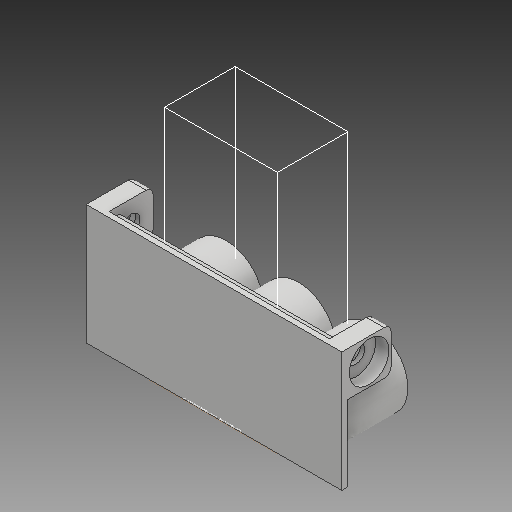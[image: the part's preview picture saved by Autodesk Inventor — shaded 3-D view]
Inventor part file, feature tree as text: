
AUTODESK INVENTOR PART (.ipt)
format: ipt  version: 2018 (Build 220112000, 112)  size: 880,640 bytes
history: native  units: mm
features: sketch x33, extrude x29, fillet x3
ambient origin geometry x8: Origin, YZ Plane, XZ Plane, XY Plane, X Axis, Y Axis, Z Axis, Center Point
bodies: Solid1 (feature_tree)
feature tree (65):
  extrude  "Extrusion1"  Depth=80.0mm
  extrude  "Extrusion2"  Depth=12.0mm
  sketch  "Sketch3"  dims[d5=12.0mm d6=14.5mm]
  extrude  "Extrusion3"  Depth=12.0mm
  extrude  "Extrusion4"  Depth=2.0mm
  extrude  "Extrusion5"  Depth=0.5mm TaperAngle=0.0deg
  sketch  "Sketch7"  dims[d15=10.0mm d16=25.0mm]
  extrude  "Extrusion6"  Depth=25.0mm
  extrude  "Extrusion7"  Depth=25.0mm
  extrude  "Extrusion8"  Depth=10.0mm
  fillet  "Fillet1"  Radius=10.0mm
  fillet  "Fillet2"  Radius=10.0mm
  extrude  "Extrusion9"  Depth=7.5mm TaperAngle=0.0deg
  extrude  "Extrusion10"  Depth=3.0mm
  fillet  "Fillet3"  Radius=3.0mm
  extrude  "Extrusion11"  Depth=21.0mm
  extrude  "Extrusion12"  Depth=41.0mm
  extrude  "Extrusion13"  Depth=42.0mm
  extrude  "Extrusion14"  Depth=38.0mm
  extrude  "Extrusion15"  Depth=45.0mm TaperAngle=0.0deg
  extrude  "Extrusion16"  Depth=3.0mm TaperAngle=0.0deg
  extrude  "Extrusion17"  Depth=3.0mm
  extrude  "Extrusion18"  Depth=39.5mm
  extrude  "Extrusion19"  Depth=45.0mm
  extrude  "Extrusion20"  Depth=125.0mm
  extrude  "Extrusion21"  Depth=1.0mm
  sketch  "Sketch24"  dims[d65=66.0mm d66=3.5mm d67=0.0mm]
  extrude  "Extrusion22"  Depth=10.0mm TaperAngle=0.0deg
  extrude  "Extrusion23"  Depth=12.0mm
  extrude  "Extrusion24"  Depth=3.5mm TaperAngle=0.0deg
  extrude  "Extrusion25"  Depth=2.0mm
  extrude  "Extrusion26"  Depth=2.0mm TaperAngle=0.0deg
  sketch  "Sketch30"  dims[d81=4.0mm]
  extrude  "Extrusion27"  Depth=16.0mm
  extrude  "Extrusion28"  Depth=2.0mm
  extrude  "Extrusion29"  Depth=3.5mm TaperAngle=0.0deg
  sketch  "Sketch1"  dims[d0=145.0mm d1=80.0mm]
  sketch  "Sketch2"  dims[d2=3.0mm d3=0.0mm d4=12.0mm]
  sketch  "Sketch4"  dims[d7=2.0mm d8=2.0mm]
  sketch  "Sketch5"  dims[d9=6.0mm d10=0.0mm d11=0.5mm d12=0.0mm]
  sketch  "Sketch6"  dims[d13=10.0mm d14=25.0mm]
  sketch  "Sketch8"  dims[d17=25.0mm d18=0.0mm d19=22.5mm d20=10.0mm d21=0.0mm d22=10.0mm]
  sketch  "Sketch9"  dims[d23=2.5mm d24=0.0mm d25=7.5mm d26=0.0mm]
  sketch  "Sketch10"  dims[d27=10.0mm d28=0.0mm d29=4.0mm d30=3.0mm]
  sketch  "Sketch11"  dims[d31=1.0mm d32=21.0mm]
  sketch  "Sketch12"  dims[d33=38.0mm d34=41.0mm]
  sketch  "Sketch13"  dims[d35=38.0mm d36=42.0mm]
  sketch  "Sketch14"  dims[d37=41.0mm d38=38.0mm]
  sketch  "Sketch15"  dims[d39=42.0mm d40=45.0mm d41=0.0mm]
  sketch  "Sketch16"  dims[d42=12.5mm d43=3.0mm d44=0.0mm]
  sketch  "Sketch17"  dims[d45=3.0mm d46=39.5mm]
  sketch  "Sketch18"  dims[d47=39.5mm d48=39.5mm]
  sketch  "Sketch19"  dims[d49=45.0mm d50=0.0mm d51=7.25mm]
  sketch  "Sketch20"  dims[d52=4.0mm d53=7.75mm d54=0.0mm d55=0.0mm d56=125.0mm]
  sketch  "Sketch21"  dims[d57=10.0mm d58=0.0mm d59=1.0mm]
  sketch  "Sketch22"  dims[d60=14.5mm d61=10.0mm d62=0.0mm]
  sketch  "Sketch23"  dims[d63=16.0mm d64=12.0mm]
  sketch  "Sketch25"  dims[d68=4.0mm d69=2.0mm]
  sketch  "Sketch26"  dims[d70=4.0mm d71=2.0mm d72=0.0mm]
  sketch  "Sketch27"  dims[d73=2.0mm d74=0.0mm d75=16.0mm]
  sketch  "Sketch28"  dims[d76=2.0mm d77=2.0mm]
  sketch  "Sketch29"  dims[d78=2.0mm d79=3.5mm d80=0.0mm]
  sketch  "Sketch31"  dims[d82=4.0mm]
  sketch  "Sketch32"  dims[d83=4.0mm]
  sketch  "Sketch33"  dims[d84=2.0mm d85=0.0mm d86=15.5mm d87=150.0mm d88=0.0mm d89=12.0mm d90=16.0mm d91=5.0mm d92=16.0mm d93=5.0mm d94=12.0mm d95=3.0mm d96=43.0mm d97=0.0mm d98=43.0mm d99=0.0mm d100=38.75mm d101=38.75mm d102=5.0mm d103=0.0mm d104=500.0mm d105=0.0mm d106=45.0mm d107=0.0mm d108=45.0mm d109=0.0mm d110=38.75mm d111=38.75mm d112=45.0mm d113=0.0mm d114=3.5mm d115=0.0mm d116=43.0mm d117=0.0mm]
